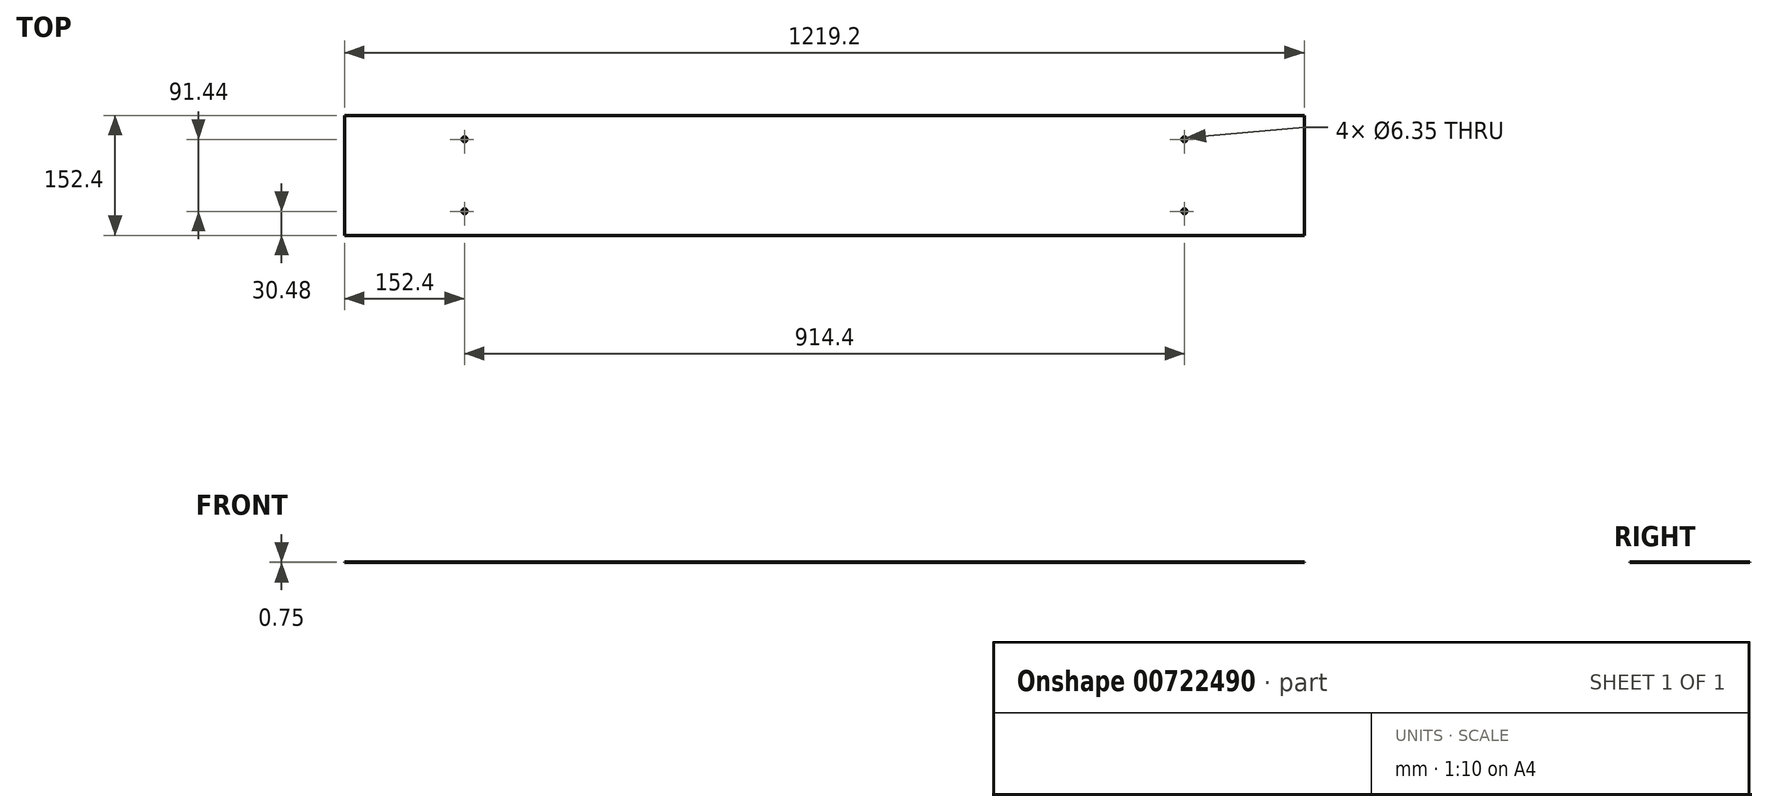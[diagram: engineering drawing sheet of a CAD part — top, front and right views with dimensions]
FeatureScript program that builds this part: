
annotation { "Feature Type Name" : "Feature", "Feature Type Description" : "" }
export const myFeature = defineFeature(function(context is Context, id is Id, definition is map)
    precondition{}
    {
        {
            assignVariable(context, id + "F0", {"name" : "T", "anyValue" : .75});
        }
        {
            var Q0;
            Q0=qCreatedBy(makeId("Top.planeOp"),FACE);
            var sketch = newSketch(context, id + "F1", { "sketchPlane" : qUnion([Q0])});
            skLineSegment(sketch, "E0.bottom", {"start": v(-609.6, 76.2) * mm, "end": v(609.6, 76.2) * mm});
            skLineSegment(sketch, "E0.top", {"start": v(-609.6, -76.2) * mm, "end": v(609.6, -76.2) * mm});
            skLineSegment(sketch, "E0.left", {"start": v(-609.6, 76.2) * mm, "end": v(-609.6, -76.2) * mm});
            skLineSegment(sketch, "E0.right", {"start": v(609.6, 76.2) * mm, "end": v(609.6, -76.2) * mm});
            skCircle(sketch, "E1", {"center": v(-457.2, 45.72) * mm, "radius": 3.18 * mm});
            skCircle(sketch, "E2", {"center": v(-457.2, -45.72) * mm, "radius": 3.17 * mm});
            skCircle(sketch, "E3", {"center": v(457.2, 45.72) * mm, "radius": 3.17 * mm});
            skCircle(sketch, "E4", {"center": v(457.2, -45.72) * mm, "radius": 3.17 * mm});
            skSolve(sketch);
        }
        {
            var Q0;
            Q0 = qSketchRegion(id + "F1", true);
            extrude(context, id + "F2", {"entities" : qUnion([Q0]), "depth" : (getVariable(context, 'T')) * mm, "offsetDistance" : 25.4 * mm});
        }
    });
